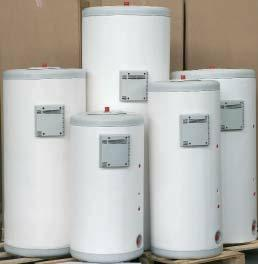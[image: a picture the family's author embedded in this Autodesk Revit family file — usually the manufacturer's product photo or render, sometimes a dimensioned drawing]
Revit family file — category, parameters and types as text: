
# Revit family: CV-200-M1S_CC01704
name_source: partatom
category: Aparatos eléctricos
revit_build: Autodesk Revit 2016 (Build: 20150220_1215(x64)
units: mm (PartAtom-declared; Revit-internal decimal feet)

## family parameters
Compartido = No
Corte con vacíos al cargar = No
Número OmniClass = 23.80.00.00
Punto de cálculo de habitación = No
Se basa en plano de trabajo = No
Siempre vertical = Sí
Título OmniClass = Electric Power and Lighting

## types (1)
- Interacumuladores CV-M1S
    Clase eficiencia energética = B
    Costo = 0 $
    Código de montaje = CC01704
    Descripción = INTERACUMULADOR CON SERPENTIN FIJO
    Dimensiones = 620 x 1207 mm
    Fabricante = SALVADOR ESCODA
    Imagen de tipo = CV-M1S.jpg
    Modelo = CV 200 M1S
    Peso vacío (aprox.) = 65 Kg
    Presión máx. depósito = 8 bar
    Pérdidas estáticas = 56 W
    Superfície intercambiador = 0,8 m2
    Temperatura máx. ACS = 90 ºC
    Temperatura máx. circuito calentamiento = 200 ºC
    URL = www.salvadorescoda.com
    Volúmen = 200 l
